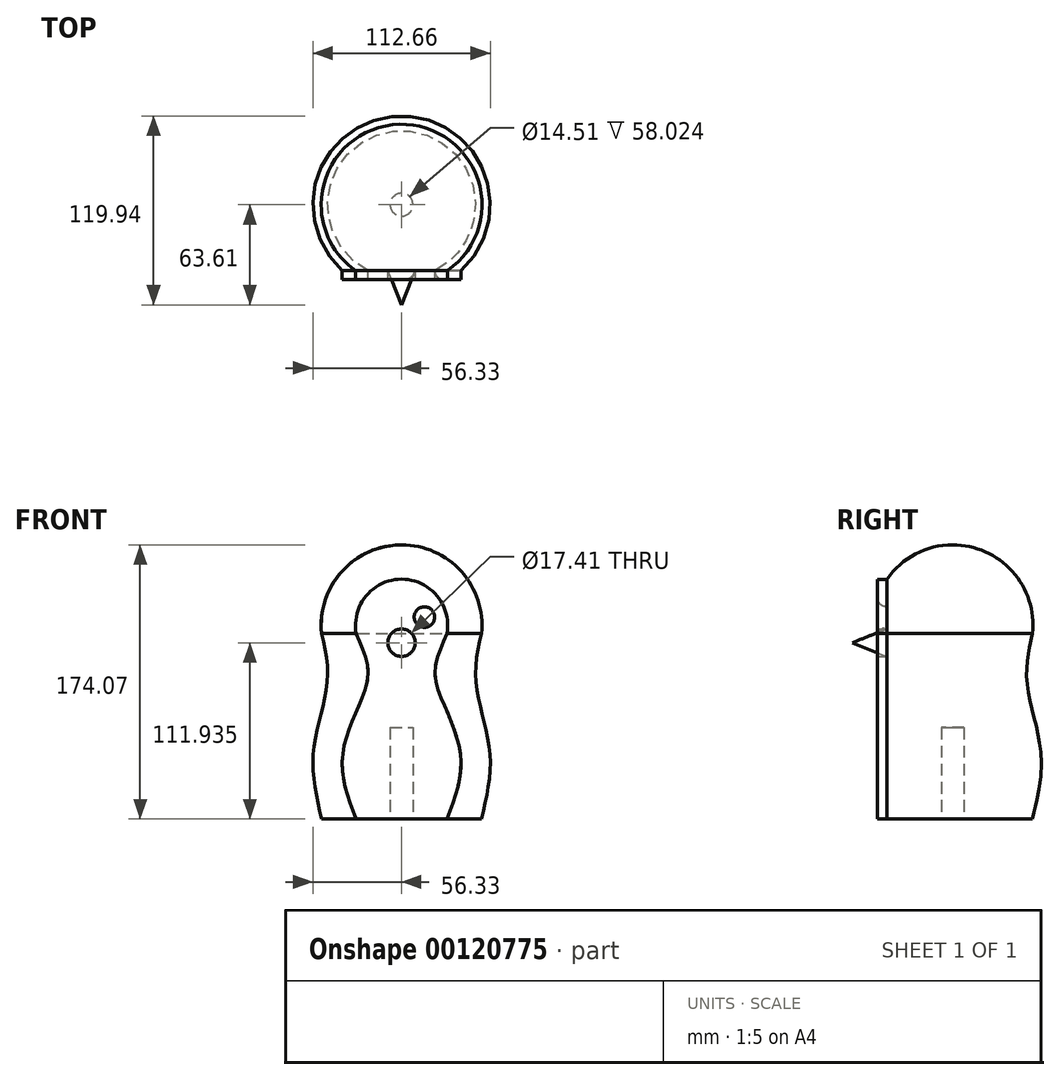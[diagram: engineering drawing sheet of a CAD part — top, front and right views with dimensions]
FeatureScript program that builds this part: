
annotation { "Feature Type Name" : "Feature", "Feature Type Description" : "" }
export const myFeature = defineFeature(function(context is Context, id is Id, definition is map)
    precondition{}
    {
        {
            var Q0;
            Q0=qCreatedBy(makeId("Front.planeOp"),FACE);
            var sketch = newSketch(context, id + "F0", { "sketchPlane" : qUnion([Q0])});
            skLineSegment(sketch, "E0", {"start": v(0, 0) * mm, "end": v(-44.47, 0) * mm});
            skFitSpline(sketch, "E1", {"points": [v(-44.47, 0) * mm, v(-49.12, 36.1) * mm, v(-41.3, 76.56) * mm, v(-44.47, 103.09) * mm], "startDerivative": vector(-23.18, 103.05) * mm, "endDerivative": vector(-19.66, 84.12) * mm});
            skArc(sketch, "E2", {"start": v(0, 152.4) * mm, "mid": v(-33.2, 137.63) * mm, "end": v(-44.47, 103.09) * mm});
            skLineSegment(sketch, "E3", {"start": v(0, 0) * mm, "end": v(0, 152.4) * mm});
            skPoint(sketch, "E4.orphan", {"position": v(44.47, 103.09) * mm});
            skLineSegment(sketch, "E5", {"start": v(-44.47, 103.09) * mm, "end": v(-44.47, 0) * mm, "construction": true});
            skPoint(sketch, "E6", {"position": v(-44.47, 59.82) * mm});
            skPoint(sketch, "E7", {"position": v(-41.15, 83.36) * mm});
            skPoint(sketch, "E8", {"position": v(-49.02, 24.5) * mm});
            skLineSegment(sketch, "E9.left", {"start": v(-44.47, 0) * mm, "end": v(-44.47, -6.35) * mm, "construction": true});
            skFitSpline(sketch, "E10.0", {"points": [v(-38.27, 1.4) * mm, v(-38.76, 3.56) * mm, v(-39.75, 7.85) * mm, v(-41.11, 14.14) * mm, v(-42.2, 20.33) * mm, v(-42.78, 25.45) * mm, v(-42.98, 29.55) * mm, v(-42.97, 32.11) * mm, v(-42.89, 34.18) * mm, v(-42.78, 35.73) * mm, v(-42.63, 37.3) * mm, v(-42.37, 39.44) * mm, v(-41.94, 42.18) * mm, v(-41.08, 46.69) * mm, v(-39.74, 52.48) * mm, v(-37.97, 59.57) * mm, v(-36.6, 65.52) * mm, v(-35.7, 70.27) * mm, v(-35.27, 73.23) * mm, v(-35, 75.6) * mm, v(-34.82, 77.96) * mm, v(-34.72, 80.84) * mm, v(-34.8, 84.17) * mm, v(-35.04, 87.38) * mm, v(-35.4, 90.49) * mm, v(-36.04, 94.48) * mm, v(-37.03, 99.23) * mm, v(-37.88, 102.8) * mm, v(-38.28, 104.53) * mm]});
            skArc(sketch, "E10.1", {"start": v(0, 146.05) * mm, "mid": v(-28.35, 133.52) * mm, "end": v(-38.19, 104.13) * mm});
            skLineSegment(sketch, "E11", {"start": v(-44.47, -6.35) * mm, "end": v(-6.35, -6.35) * mm, "construction": true});
            skLineSegment(sketch, "E12", {"start": v(-6.35, -6.35) * mm, "end": v(0, -6.35) * mm, "construction": true});
            skLineSegment(sketch, "E13", {"start": v(-6.35, -6.35) * mm, "end": v(-6.35, 0) * mm, "construction": true});
            skLineSegment(sketch, "E14", {"start": v(-38.27, 1.4) * mm, "end": v(-38.27, 0) * mm});
            skSolve(sketch);
        }
        {
            var Q0;
            Q0 = qSketchRegion(id + "F0", true);
            var Q1;
            Q1=sQuery(id+"F0.wireOp",EDGE,"E3");
            revolve(context, id + "F1", {"entities" : qUnion([Q0]), "axis" : qUnion([Q1]), "revolveType" : RevolveType.FULL});
        }
        {
            var Q0;
            Q0=qCreatedBy(makeId("Top.planeOp"),FACE);
            var sketch = newSketch(context, id + "F2", { "sketchPlane" : qUnion([Q0])});
            skCircle(sketch, "E15", {"center": v(0, 0) * mm, "radius": 44.7 * mm, "construction": true});
            skCircle(sketch, "E16.0", {"center": v(0, 0) * mm, "radius": 44.47 * mm, "construction": true});
            skLineSegment(sketch, "E17", {"start": v(0, 0) * mm, "end": v(0, -44.47) * mm, "construction": true});
            skLineSegment(sketch, "E18", {"start": v(-25.2, -36.64) * mm, "end": v(25.6, -36.64) * mm});
            skLineSegment(sketch, "E19", {"start": v(-25.2, -36.64) * mm, "end": v(-46.78, -36.64) * mm});
            skLineSegment(sketch, "E20.bottom", {"start": v(-46.78, -36.64) * mm, "end": v(42.12, -36.64) * mm});
            skLineSegment(sketch, "E20.top", {"start": v(-46.78, -67.12) * mm, "end": v(42.12, -67.12) * mm});
            skLineSegment(sketch, "E20.left", {"start": v(-46.78, -36.64) * mm, "end": v(-46.78, -67.12) * mm});
            skLineSegment(sketch, "E20.right", {"start": v(42.12, -36.64) * mm, "end": v(42.12, -67.12) * mm});
            skSolve(sketch);
        }
        {
            var Q0;
            Q0 = qSketchRegion(id + "F2", true);
            extrude(context, id + "F3", {"entities" : qUnion([Q0]), "operationType" : NewBodyOperationType.REMOVE, "depth" : 177.8 * mm});
        }
        {
            var Q0;
            Q0=makeQuery(id+"F3.boolean.opBoolean","COPY",FACE,{"derivedFrom":makeQuery(id+"F3.opExtrude","SWEPT_FACE",FACE,{"disambiguationData":[OSD([sQuery(id+"F2.wireOp",EDGE,"E20.bottom")])]})});
            var sketch = newSketch(context, id + "F4", { "sketchPlane" : qUnion([Q0])});
            skLineSegment(sketch, "E21", {"start": v(0, 0) * mm, "end": v(0, 133.3) * mm, "construction": true});
            skPoint(sketch, "E22", {"position": v(0, 112.22) * mm});
            skLineSegment(sketch, "E23", {"start": v(-12.7, 112.22) * mm, "end": v(12.7, 112.22) * mm, "construction": true});
            skCircle(sketch, "E24", {"center": v(-12.7, 112.22) * mm, "radius": 5.72 * mm});
            skCircle(sketch, "E25", {"center": v(0, 98) * mm, "radius": 7.62 * mm});
            skCircle(sketch, "E26.MirrorC", {"center": v(12.7, 112.22) * mm, "radius": 5.72 * mm});
            skLineSegment(sketch, "E27", {"start": v(-12.7, 106.5) * mm, "end": v(-12.7, 112.22) * mm, "construction": true});
            skLineSegment(sketch, "E28", {"start": v(-12.7, 112.22) * mm, "end": v(-12.7, 117.94) * mm, "construction": true});
            skSolve(sketch);
        }
        {
            var Q0;
            Q0=makeQuery(id+"F4.imprint","IMPRINT",FACE,{"disambiguationData":[TD([[makeQuery(id+"F4.imprint","IMPRINT",EDGE,{"derivedFrom":sQuery(id+"F4.wireOp",EDGE,"E25")}),1.0]])]});
            extrude(context, id + "F5", {"entities" : qUnion([Q0]), "operationType" : NewBodyOperationType.ADD, "depth" : 19.05 * mm});
        }
        {
            var Q0;
            Q0=makeQuery(id+"F5.opExtrude","CAP_EDGE",EDGE,{"disambiguationData":[OSD([sQuery(id+"F4.wireOp",EDGE,"E25")])],"isStart":false});
            chamfer(context, id + "F6", {"entities" : qUnion([Q0]), "chamferType" : ChamferType.OFFSET_ANGLE, "width" : 7.62 * mm, "oppositeDirection" : false, "angle" : 68 * degree, "tangentPropagation" : true});
        }
        {
            var Q0;
            Q0=makeQuery(id+"F4.imprint","IMPRINT",FACE,{"disambiguationData":[TD([[makeQuery(id+"F4.imprint","IMPRINT",EDGE,{"derivedFrom":sQuery(id+"F4.wireOp",EDGE,"E24")}),1.0]])]});
            var Q1;
            Q1=makeQuery(id+"F4.imprint","IMPRINT",FACE,{"disambiguationData":[TD([[makeQuery(id+"F4.imprint","IMPRINT",EDGE,{"derivedFrom":sQuery(id+"F4.wireOp",EDGE,"E26.MirrorC")}),-1.0]])]});
            extrude(context, id + "F7", {"entities" : qUnion([Q0, Q1]), "operationType" : NewBodyOperationType.ADD, "depth" : 5.08 * mm});
        }
        {
            var Q0;
            Q0=makeQuery(id+"F7.opExtrude","CAP_EDGE",EDGE,{"disambiguationData":[OSD([sQuery(id+"F4.wireOp",EDGE,"E24")])],"isStart":false});
            var Q1;
            Q1=makeQuery(id+"F7.opExtrude","CAP_EDGE",EDGE,{"disambiguationData":[OSD([sQuery(id+"F4.wireOp",EDGE,"E26.MirrorC")])],"isStart":false});
            fillet(context, id + "F8", {"entities" : qUnion([Q0, Q1]), "radius" : 5.08 * mm, "tangentPropagation" : true, "allowEdgeOverflow" : false});
        }
        {
            var Q0;
            Q0=makeQuery(id+"F1.opRevolve","SWEPT_FACE",FACE,{"disambiguationData":[OSD([sQuery(id+"F0.wireOp",EDGE,"E0")])]});
            var sketch = newSketch(context, id + "F9", { "sketchPlane" : qUnion([Q0])});
            skCircle(sketch, "E29", {"center": v(0, 0) * mm, "radius": 6.35 * mm});
            skSolve(sketch);
        }
        {
            var Q0;
            Q0 = qSketchRegion(id + "F9", true);
            extrude(context, id + "F10", {"entities" : qUnion([Q0]), "operationType" : NewBodyOperationType.REMOVE, "oppositeDirection" : true, "depth" : 50.8 * mm});
        }
        {
            var Q0;
            Q0=makeQuery(id+"F1.opRevolve","SWEPT_BODY",BODY,{"disambiguationData":[OSD([sQuery(id+"F0.wireOp",EDGE,"E0"),sQuery(id+"F0.wireOp",EDGE,"E1"),sQuery(id+"F0.wireOp",EDGE,"E2"),sQuery(id+"F0.wireOp",EDGE,"E3"),sQuery(id+"F0.wireOp",EDGE,"E9.left"),sQuery(id+"F0.wireOp",EDGE,"E11"),sQuery(id+"F0.wireOp",EDGE,"E13")])]});
            var Q1;
            Q1=qCreatedBy(makeId("Origin.pointOp"),VERTEX);
            var Q2;
            Q2=qCreatedBy(makeId("Origin.pointOp"),VERTEX);
            transform(context, id + "F11", {"entities" : qUnion([Q0]), "transformType" : TransformType.SCALE_UNIFORMLY, "scale" : 1.14, "scalePoint" : qUnion([Q2]), "makeCopy" : false});
        }
    });
